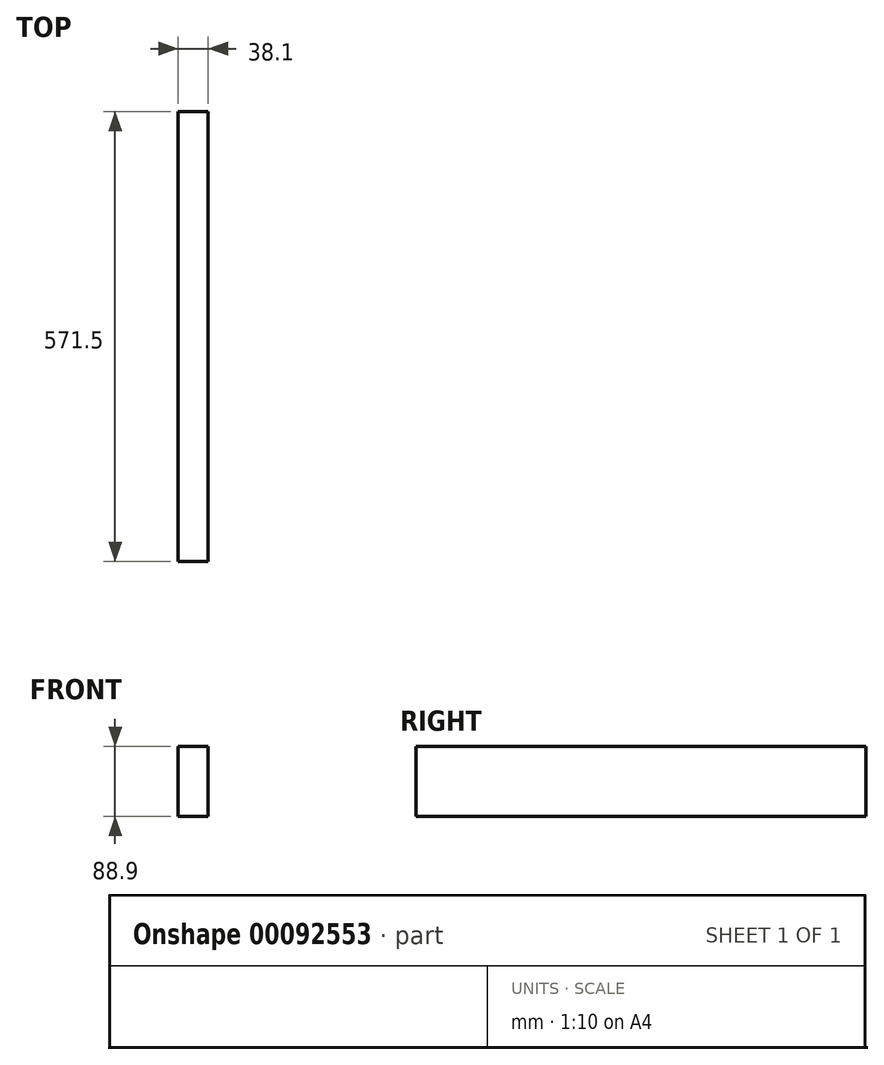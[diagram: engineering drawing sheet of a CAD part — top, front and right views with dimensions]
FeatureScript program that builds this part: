
annotation { "Feature Type Name" : "Feature", "Feature Type Description" : "" }
export const myFeature = defineFeature(function(context is Context, id is Id, definition is map)
    precondition{}
    {
        {
            var Q0;
            Q0=qCreatedBy(makeId("Front.planeOp"),FACE);
            var sketch = newSketch(context, id + "F0", { "sketchPlane" : qUnion([Q0])});
            skLineSegment(sketch, "E0.bottom", {"start": v(0, 0) * mm, "end": v(38.1, 0) * mm});
            skLineSegment(sketch, "E0.top", {"start": v(0, 88.9) * mm, "end": v(38.1, 88.9) * mm});
            skLineSegment(sketch, "E0.left", {"start": v(0, 0) * mm, "end": v(0, 88.9) * mm});
            skLineSegment(sketch, "E0.right", {"start": v(38.1, 0) * mm, "end": v(38.1, 88.9) * mm});
            skSolve(sketch);
        }
        {
            var Q0;
            Q0=makeQuery(id+"F0.imprint","IMPRINT",FACE,{"disambiguationData":[TD([[makeQuery(id+"F0.imprint","IMPRINT",EDGE,{"derivedFrom":sQuery(id+"F0.wireOp",EDGE,"E0.bottom")}),1.0]])]});
            extrude(context, id + "F1", {"entities" : qUnion([Q0]), "oppositeDirection" : true, "depth" : 571.5 * mm});
        }
    });
